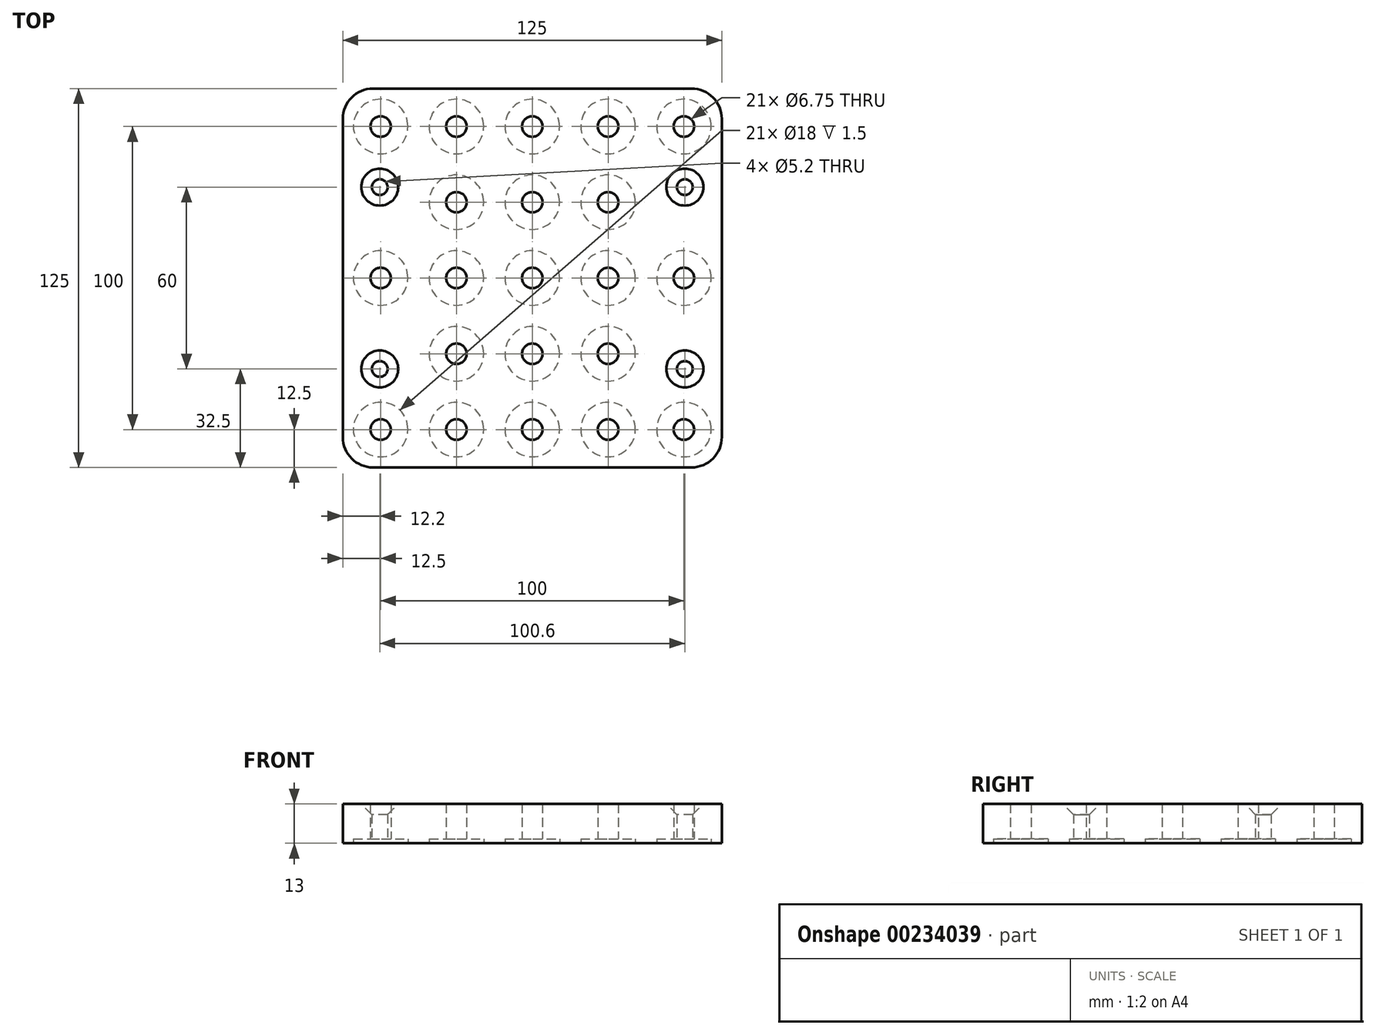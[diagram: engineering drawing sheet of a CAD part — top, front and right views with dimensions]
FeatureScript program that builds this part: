
annotation { "Feature Type Name" : "Feature", "Feature Type Description" : "" }
export const myFeature = defineFeature(function(context is Context, id is Id, definition is map)
    precondition{}
    {
        {
            var Q0;
            Q0=qCreatedBy(makeId("Top.planeOp"),FACE);
            var sketch = newSketch(context, id + "F0", { "sketchPlane" : qUnion([Q0])});
            skLineSegment(sketch, "E0.bottom", {"start": v(52.5, -62.5) * mm, "end": v(-52.5, -62.5) * mm});
            skLineSegment(sketch, "E0.top", {"start": v(52.5, 62.5) * mm, "end": v(-52.5, 62.5) * mm});
            skLineSegment(sketch, "E0.right", {"start": v(-62.5, -52.5) * mm, "end": v(-62.5, 52.5) * mm});
            skPoint(sketch, "E1.visualSharp", {"position": v(-62.5, 62.5) * mm});
            skArc(sketch, "E1.filletArc", {"start": v(-52.5, 62.5) * mm, "mid": v(-59.57, 59.57) * mm, "end": v(-62.5, 52.5) * mm});
            skPoint(sketch, "E2.visualSharp", {"position": v(87.5, 62.5) * mm});
            skArc(sketch, "E2.filletArc", {"start": v(62.5, 52.5) * mm, "mid": v(59.57, 59.57) * mm, "end": v(52.5, 62.5) * mm});
            skPoint(sketch, "E3.visualSharp", {"position": v(87.5, -62.5) * mm});
            skArc(sketch, "E3.filletArc", {"start": v(52.5, -62.5) * mm, "mid": v(59.57, -59.57) * mm, "end": v(62.5, -52.5) * mm});
            skPoint(sketch, "E4.visualSharp", {"position": v(-62.5, -62.5) * mm});
            skArc(sketch, "E4.filletArc", {"start": v(-62.5, -52.5) * mm, "mid": v(-59.57, -59.57) * mm, "end": v(-52.5, -62.5) * mm});
            skLineSegment(sketch, "E5.bottom", {"start": v(50.3, -30) * mm, "end": v(-50.3, -30) * mm, "construction": true});
            skLineSegment(sketch, "E5.top", {"start": v(50.3, 30) * mm, "end": v(-50.3, 30) * mm, "construction": true});
            skLineSegment(sketch, "E5.right", {"start": v(-50.3, -30) * mm, "end": v(-50.3, 30) * mm, "construction": true});
            skCircle(sketch, "E6", {"center": v(-50.3, 30) * mm, "radius": 2.6 * mm});
            skCircle(sketch, "E7", {"center": v(50.3, 30) * mm, "radius": 2.6 * mm});
            skCircle(sketch, "E8", {"center": v(50.3, -30) * mm, "radius": 2.6 * mm});
            skCircle(sketch, "E9", {"center": v(-50.3, -30) * mm, "radius": 2.6 * mm});
            skLineSegment(sketch, "E10", {"start": v(62.5, 52.5) * mm, "end": v(62.5, -52.5) * mm});
            skCircle(sketch, "E11.2.0.0", {"center": v(0, 50) * mm, "radius": 3.38 * mm});
            skCircle(sketch, "E11.2.1.0", {"center": v(0, 25) * mm, "radius": 3.38 * mm});
            skCircle(sketch, "E11.2.2.0", {"center": v(0, 0) * mm, "radius": 3.38 * mm});
            skCircle(sketch, "E11.2.3.0", {"center": v(0, -25) * mm, "radius": 3.38 * mm});
            skCircle(sketch, "E11.2.4.0", {"center": v(0, -50) * mm, "radius": 3.38 * mm});
            skCircle(sketch, "E12.1.0.0", {"center": v(25, 25) * mm, "radius": 3.38 * mm});
            skCircle(sketch, "E12.1.0.1", {"center": v(25, 50) * mm, "radius": 3.38 * mm});
            skCircle(sketch, "E12.1.0.2", {"center": v(25, -25) * mm, "radius": 3.38 * mm});
            skCircle(sketch, "E12.1.0.3", {"center": v(25, -50) * mm, "radius": 3.38 * mm});
            skCircle(sketch, "E12.1.0.4", {"center": v(25, 0) * mm, "radius": 3.38 * mm});
            skCircle(sketch, "E12.2.0.1", {"center": v(50, 50) * mm, "radius": 3.38 * mm});
            skCircle(sketch, "E12.2.0.3", {"center": v(50, -50) * mm, "radius": 3.38 * mm});
            skCircle(sketch, "E12.2.0.4", {"center": v(50, 0) * mm, "radius": 3.38 * mm});
            skLineSegment(sketch, "E12.direction1", {"start": v(0, -50) * mm, "end": v(25, -50) * mm, "construction": true});
            skCircle(sketch, "E13.1.0.0", {"center": v(-25, 25) * mm, "radius": 3.38 * mm});
            skCircle(sketch, "E13.1.0.1", {"center": v(-25, -25) * mm, "radius": 3.38 * mm});
            skCircle(sketch, "E13.1.0.2", {"center": v(-25, 0) * mm, "radius": 3.38 * mm});
            skCircle(sketch, "E13.1.0.3", {"center": v(-25, 50) * mm, "radius": 3.38 * mm});
            skCircle(sketch, "E13.1.0.4", {"center": v(-25, -50) * mm, "radius": 3.38 * mm});
            skCircle(sketch, "E13.2.0.2", {"center": v(-50, 0) * mm, "radius": 3.38 * mm});
            skCircle(sketch, "E13.2.0.3", {"center": v(-50, 50) * mm, "radius": 3.38 * mm});
            skCircle(sketch, "E13.2.0.4", {"center": v(-50, -50) * mm, "radius": 3.38 * mm});
            skLineSegment(sketch, "E13.direction1", {"start": v(0, -50) * mm, "end": v(-25, -50) * mm, "construction": true});
            skSolve(sketch);
        }
        {
            var Q0;
            Q0 = qSketchRegion(id + "F0", true);
            extrude(context, id + "F1", {"entities" : qUnion([Q0]), "depth" : 13 * mm});
        }
        {
            var Q0;
            Q0=makeQuery(id+"F1.opExtrude","CAP_EDGE",EDGE,{"disambiguationData":[OSD([sQuery(id+"F0.wireOp",EDGE,"E6")])],"isStart":false});
            var Q1;
            Q1=makeQuery(id+"F1.opExtrude","CAP_EDGE",EDGE,{"disambiguationData":[OSD([sQuery(id+"F0.wireOp",EDGE,"E7")])],"isStart":false});
            var Q2;
            Q2=makeQuery(id+"F1.opExtrude","CAP_EDGE",EDGE,{"disambiguationData":[OSD([sQuery(id+"F0.wireOp",EDGE,"E8")])],"isStart":false});
            var Q3;
            Q3=makeQuery(id+"F1.opExtrude","CAP_EDGE",EDGE,{"disambiguationData":[OSD([sQuery(id+"F0.wireOp",EDGE,"E9")])],"isStart":false});
            chamfer(context, id + "F2", {"entities" : qUnion([Q0, Q1, Q2, Q3]), "width" : 3.5 * mm, "tangentPropagation" : true});
        }
        {
            var Q0;
            Q0=makeQuery(id+"F1.opExtrude","CAP_FACE",FACE,{"disambiguationData":[OSD([sQuery(id+"F0.wireOp",EDGE,"E0.bottom"),sQuery(id+"F0.wireOp",EDGE,"E0.top"),sQuery(id+"F0.wireOp",EDGE,"E0.right"),sQuery(id+"F0.wireOp",EDGE,"E1.filletArc"),sQuery(id+"F0.wireOp",EDGE,"E2.filletArc"),sQuery(id+"F0.wireOp",EDGE,"E3.filletArc"),sQuery(id+"F0.wireOp",EDGE,"E4.filletArc"),sQuery(id+"F0.wireOp",EDGE,"E6"),sQuery(id+"F0.wireOp",EDGE,"E7"),sQuery(id+"F0.wireOp",EDGE,"E8"),sQuery(id+"F0.wireOp",EDGE,"E9"),sQuery(id+"F0.wireOp",EDGE,"E10"),sQuery(id+"F0.wireOp",EDGE,"E11.2.0.0"),sQuery(id+"F0.wireOp",EDGE,"E11.2.1.0"),sQuery(id+"F0.wireOp",EDGE,"E11.2.2.0"),sQuery(id+"F0.wireOp",EDGE,"E11.2.3.0"),sQuery(id+"F0.wireOp",EDGE,"E11.2.4.0"),sQuery(id+"F0.wireOp",EDGE,"E12.1.0.0"),sQuery(id+"F0.wireOp",EDGE,"E12.1.0.1"),sQuery(id+"F0.wireOp",EDGE,"E12.1.0.2"),sQuery(id+"F0.wireOp",EDGE,"E12.1.0.3"),sQuery(id+"F0.wireOp",EDGE,"E12.1.0.4"),sQuery(id+"F0.wireOp",EDGE,"E12.2.0.1"),sQuery(id+"F0.wireOp",EDGE,"E12.2.0.3"),sQuery(id+"F0.wireOp",EDGE,"E12.2.0.4"),sQuery(id+"F0.wireOp",EDGE,"E13.1.0.0"),sQuery(id+"F0.wireOp",EDGE,"E13.1.0.1"),sQuery(id+"F0.wireOp",EDGE,"E13.1.0.2"),sQuery(id+"F0.wireOp",EDGE,"E13.1.0.3"),sQuery(id+"F0.wireOp",EDGE,"E13.1.0.4"),sQuery(id+"F0.wireOp",EDGE,"E13.2.0.2"),sQuery(id+"F0.wireOp",EDGE,"E13.2.0.3"),sQuery(id+"F0.wireOp",EDGE,"E13.2.0.4")])],"isStart":true});
            var sketch = newSketch(context, id + "F3", { "sketchPlane" : qUnion([Q0])});
            skCircle(sketch, "E14", {"center": v(0, 50) * mm, "radius": 9 * mm});
            skCircle(sketch, "E15", {"center": v(0, 25) * mm, "radius": 9 * mm});
            skCircle(sketch, "E16", {"center": v(0, 0) * mm, "radius": 9 * mm});
            skCircle(sketch, "E17", {"center": v(0, -25) * mm, "radius": 9 * mm});
            skCircle(sketch, "E18", {"center": v(0, -50) * mm, "radius": 9 * mm});
            skCircle(sketch, "E19.1.0.0", {"center": v(25, -25) * mm, "radius": 9 * mm});
            skCircle(sketch, "E19.1.0.1", {"center": v(25, 0) * mm, "radius": 9 * mm});
            skCircle(sketch, "E19.1.0.2", {"center": v(25, 25) * mm, "radius": 9 * mm});
            skCircle(sketch, "E19.1.0.3", {"center": v(25, 50) * mm, "radius": 9 * mm});
            skCircle(sketch, "E19.1.0.4", {"center": v(25, -50) * mm, "radius": 9 * mm});
            skCircle(sketch, "E19.2.0.1", {"center": v(50, 0) * mm, "radius": 9 * mm});
            skCircle(sketch, "E19.2.0.3", {"center": v(50, 50) * mm, "radius": 9 * mm});
            skCircle(sketch, "E19.2.0.4", {"center": v(50, -50) * mm, "radius": 9 * mm});
            skLineSegment(sketch, "E19.direction1", {"start": v(0, -50) * mm, "end": v(25, -50) * mm, "construction": true});
            skCircle(sketch, "E20.1.0.0", {"center": v(-25, 0) * mm, "radius": 9 * mm});
            skCircle(sketch, "E20.1.0.1", {"center": v(-25, 25) * mm, "radius": 9 * mm});
            skCircle(sketch, "E20.1.0.2", {"center": v(-25, -25) * mm, "radius": 9 * mm});
            skCircle(sketch, "E20.1.0.3", {"center": v(-25, 50) * mm, "radius": 9 * mm});
            skCircle(sketch, "E20.1.0.4", {"center": v(-25, -50) * mm, "radius": 9 * mm});
            skCircle(sketch, "E20.2.0.0", {"center": v(-50, 0) * mm, "radius": 9 * mm});
            skCircle(sketch, "E20.2.0.3", {"center": v(-50, 50) * mm, "radius": 9 * mm});
            skCircle(sketch, "E20.2.0.4", {"center": v(-50, -50) * mm, "radius": 9 * mm});
            skLineSegment(sketch, "E20.direction1", {"start": v(0, -50) * mm, "end": v(-25, -50) * mm, "construction": true});
            skSolve(sketch);
        }
        {
            var Q0;
            Q0 = qSketchRegion(id + "F3", true);
            extrude(context, id + "F4", {"entities" : qUnion([Q0]), "operationType" : NewBodyOperationType.REMOVE, "oppositeDirection" : true, "depth" : 1.5 * mm});
        }
    });
